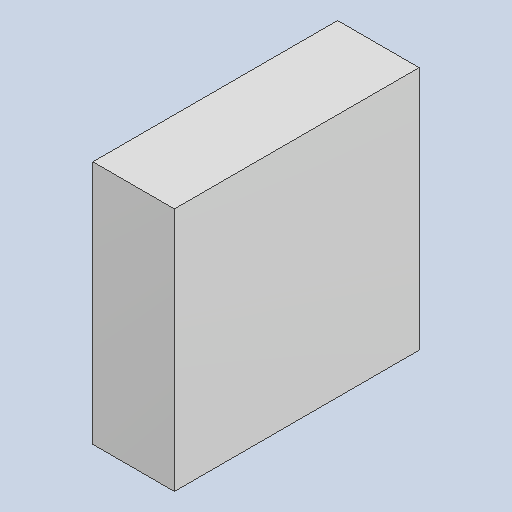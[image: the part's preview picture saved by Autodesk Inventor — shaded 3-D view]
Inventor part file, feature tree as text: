
AUTODESK INVENTOR PART (.ipt)
format: ipt  version: 2023.4 (Build 274418000, 418)  size: 81,408 bytes
history: native  units: mm
features: extrude x1
ambient origin geometry x8: Origin, YZ Plane, XZ Plane, XY Plane, X Axis, Y Axis, Z Axis, Center Point
bodies: Solid1 (feature_tree)
feature tree (1):
  extrude  "Extruded_25"  [1 undecoded]
note: 1 required parameter value undecoded (feature->parameter linkage not recoverable at this tier; creation-order binding heuristic only, values carry confidence <= 0.55)
